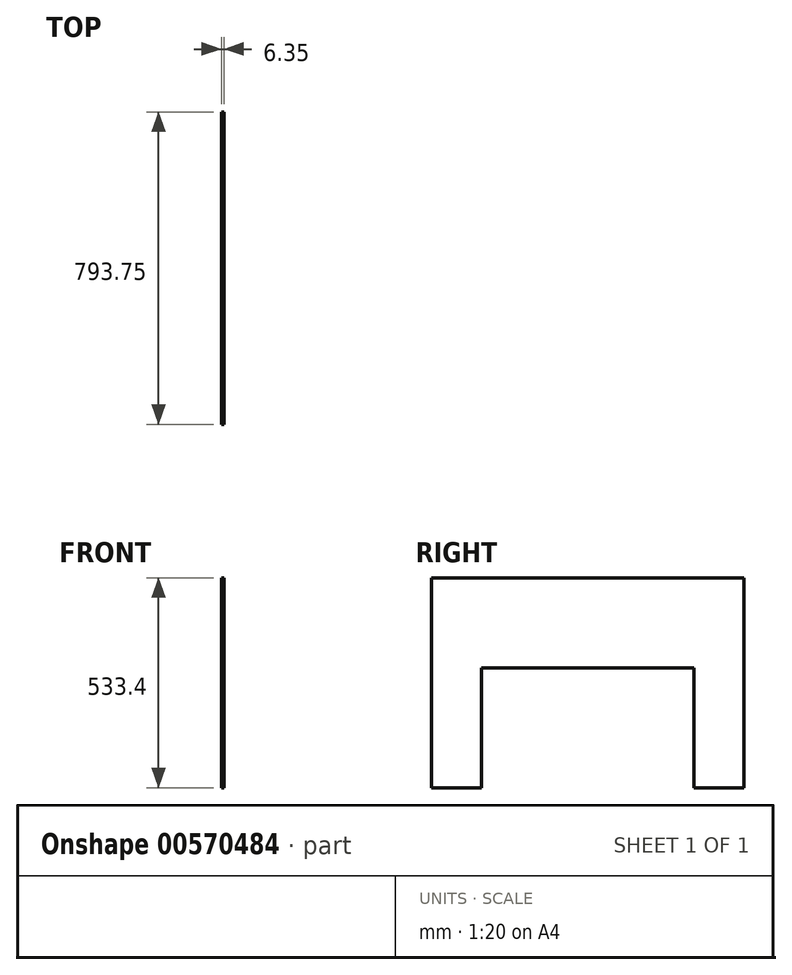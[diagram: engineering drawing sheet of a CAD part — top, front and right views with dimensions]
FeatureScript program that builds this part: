
annotation { "Feature Type Name" : "Feature", "Feature Type Description" : "" }
export const myFeature = defineFeature(function(context is Context, id is Id, definition is map)
    precondition{}
    {
        {
            var Q0;
            Q0=qCreatedBy(makeId("Right.planeOp"),FACE);
            var sketch = newSketch(context, id + "F0", { "sketchPlane" : qUnion([Q0])});
            skLineSegment(sketch, "E0.bottom", {"start": v(0, 0) * mm, "end": v(-793.75, 0) * mm});
            skLineSegment(sketch, "E0.top", {"start": v(0, -533.4) * mm, "end": v(-127, -533.4) * mm});
            skLineSegment(sketch, "E0.left", {"start": v(0, 0) * mm, "end": v(0, -533.4) * mm});
            skLineSegment(sketch, "E0.right", {"start": v(-793.75, 0) * mm, "end": v(-793.75, -533.4) * mm});
            skLineSegment(sketch, "E1.right", {"start": v(-127, -533.4) * mm, "end": v(-127, -228.6) * mm});
            skLineSegment(sketch, "E2.right", {"start": v(-666.75, -533.4) * mm, "end": v(-666.75, -228.6) * mm});
            skLineSegment(sketch, "E3.trimOffspring", {"start": v(-666.75, -533.4) * mm, "end": v(-793.75, -533.4) * mm});
            skLineSegment(sketch, "E4", {"start": v(-666.75, -228.6) * mm, "end": v(-127, -228.6) * mm});
            skSolve(sketch);
        }
        {
            var Q0;
            Q0 = qSketchRegion(id + "F0", true);
            extrude(context, id + "F1", {"entities" : qUnion([Q0]), "depth" : 6.35 * mm, "offsetDistance" : 25.4 * mm});
        }
    });
